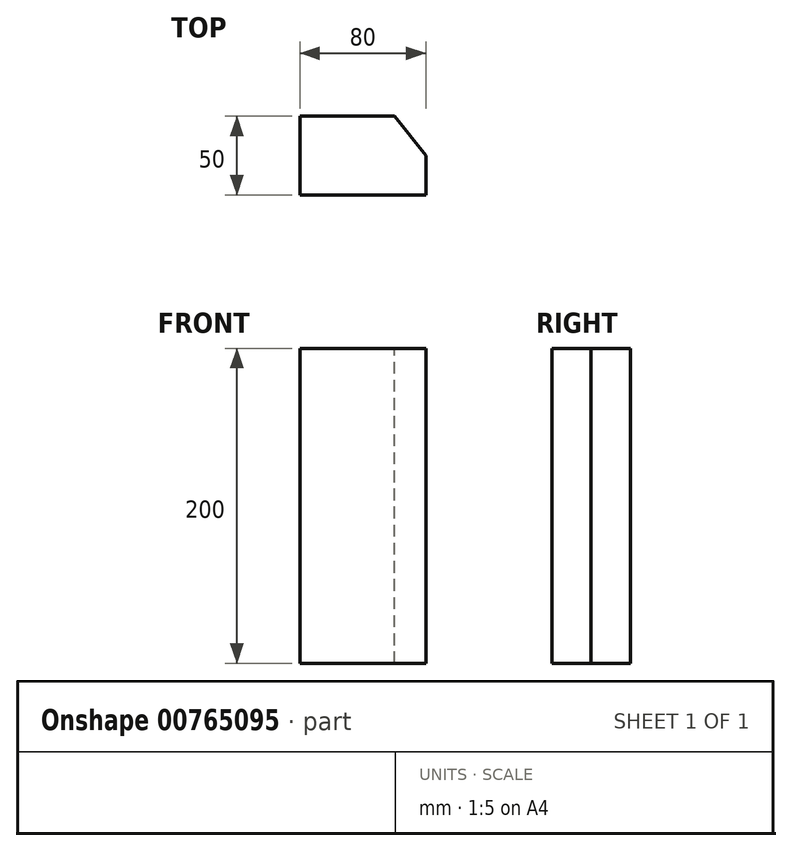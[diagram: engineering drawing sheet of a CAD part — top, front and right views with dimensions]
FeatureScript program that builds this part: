
annotation { "Feature Type Name" : "Feature", "Feature Type Description" : "" }
export const myFeature = defineFeature(function(context is Context, id is Id, definition is map)
    precondition{}
    {
        {
            var Q0;
            Q0=qCreatedBy(makeId("Top.planeOp"),FACE);
            var sketch = newSketch(context, id + "F0", { "sketchPlane" : qUnion([Q0])});
            skLineSegment(sketch, "E0.bottom", {"start": v(-40, 25) * mm, "end": v(20, 25) * mm});
            skLineSegment(sketch, "E0.top", {"start": v(-40, -25) * mm, "end": v(40, -25) * mm});
            skLineSegment(sketch, "E0.left", {"start": v(-40, 25) * mm, "end": v(-40, -25) * mm});
            skLineSegment(sketch, "E0.right", {"start": v(40, 0) * mm, "end": v(40, -25) * mm});
            skPoint(sketch, "E0.middle", {"position": v(0, 0) * mm});
            skPoint(sketch, "E1.orphan", {"position": v(40, 25) * mm});
            skLineSegment(sketch, "E2.0", {"start": v(35, -2.77) * mm, "end": v(35, -20) * mm});
            skLineSegment(sketch, "E2.3", {"start": v(-35, 20) * mm, "end": v(-35, -20) * mm});
            skLineSegment(sketch, "E2.4", {"start": v(-35, 20) * mm, "end": v(-1.43, 20) * mm});
            skLineSegment(sketch, "E3", {"start": v(35, -20) * mm, "end": v(35, -25) * mm});
            skLineSegment(sketch, "E4", {"start": v(-35, -20) * mm, "end": v(-35, -25) * mm});
            skLineSegment(sketch, "E5", {"start": v(40, 0) * mm, "end": v(20, 25) * mm});
            skSolve(sketch);
        }
        {
            var Q0;
            Q0=makeQuery(id+"F0.imprint","IMPRINT",FACE,{"disambiguationData":[TD([[makeQuery(id+"F0.imprint","IMPRINT",EDGE,{"derivedFrom":sQuery(id+"F0.wireOp",EDGE,"E2.0")}),-1.0]])]});
            var Q1;
            Q1=makeQuery(id+"F0.imprint","IMPRINT",FACE,{"disambiguationData":[TD([[makeQuery(id+"F0.imprint","IMPRINT",EDGE,{"derivedFrom":sQuery(id+"F0.wireOp",EDGE,"E0.bottom")}),-1.0]])]});
            extrude(context, id + "F1", {"entities" : qUnion([Q0, Q1]), "depth" : -5 * mm, "offsetDistance" : 25 * mm});
        }
        {
            var Q0;
            Q0 = qSketchRegion(id + "F0", true);
            extrude(context, id + "F2", {"entities" : qUnion([Q0]), "operationType" : NewBodyOperationType.ADD, "depth" : (195) * mm, "offsetDistance" : 25 * mm});
        }
    });
